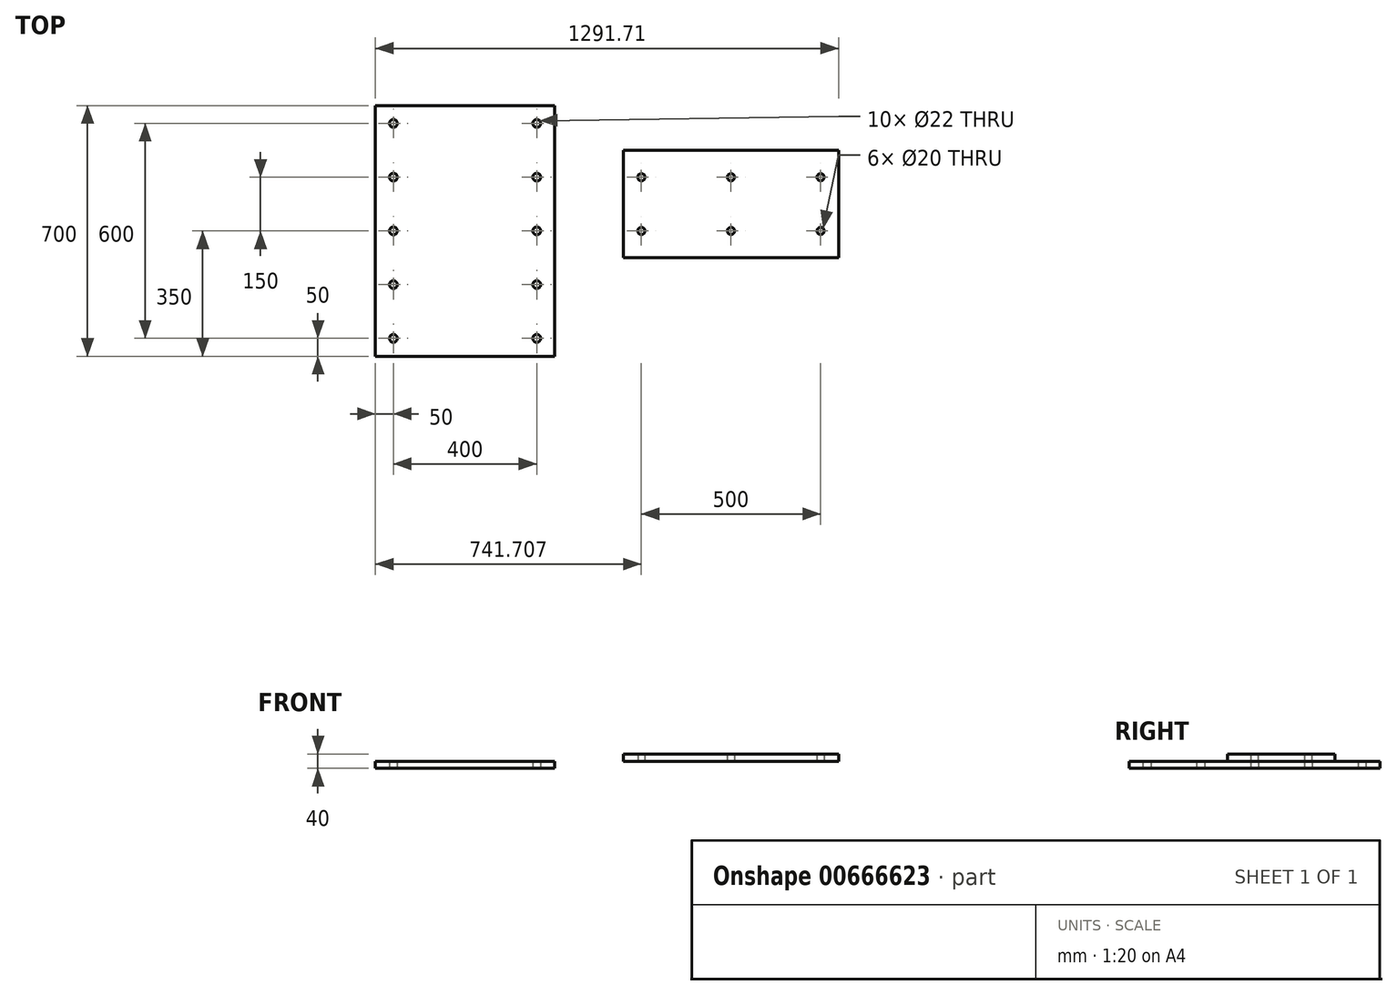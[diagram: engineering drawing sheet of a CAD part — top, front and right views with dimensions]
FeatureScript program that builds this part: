
annotation { "Feature Type Name" : "Feature", "Feature Type Description" : "" }
export const myFeature = defineFeature(function(context is Context, id is Id, definition is map)
    precondition{}
    {
        {
            var Q0;
            Q0=qCreatedBy(makeId("Top.planeOp"),FACE);
            var sketch = newSketch(context, id + "F0", { "sketchPlane" : qUnion([Q0])});
            skLineSegment(sketch, "E0.bottom", {"start": v(250, -350) * mm, "end": v(-250, -350) * mm});
            skLineSegment(sketch, "E0.top", {"start": v(250, 350) * mm, "end": v(-250, 350) * mm});
            skLineSegment(sketch, "E0.left", {"start": v(250, -350) * mm, "end": v(250, 350) * mm});
            skLineSegment(sketch, "E0.right", {"start": v(-250, -350) * mm, "end": v(-250, 350) * mm});
            skPoint(sketch, "E0.middle", {"position": v(0, 0) * mm});
            skSolve(sketch);
        }
        {
            var Q0;
            Q0=makeQuery(id+"F0.imprint","IMPRINT",FACE,{"disambiguationData":[TD([[makeQuery(id+"F0.imprint","IMPRINT",EDGE,{"derivedFrom":sQuery(id+"F0.wireOp",EDGE,"E0.bottom")}),-1.0]])]});
            var sketch = newSketch(context, id + "F1", { "sketchPlane" : qUnion([Q0])});
            skCircle(sketch, "E1", {"center": v(200, 300) * mm, "radius": 11 * mm});
            skCircle(sketch, "E2", {"center": v(200, 150) * mm, "radius": 11 * mm});
            skCircle(sketch, "E3", {"center": v(200, 0) * mm, "radius": 11 * mm});
            skCircle(sketch, "E4", {"center": v(200, -150) * mm, "radius": 11 * mm});
            skCircle(sketch, "E5", {"center": v(200, -300) * mm, "radius": 11 * mm});
            skCircle(sketch, "E6", {"center": v(-200, 300) * mm, "radius": 11 * mm});
            skCircle(sketch, "E7", {"center": v(-200, 150) * mm, "radius": 11 * mm});
            skCircle(sketch, "E8", {"center": v(-200, 0) * mm, "radius": 11 * mm});
            skCircle(sketch, "E9", {"center": v(-200, -150) * mm, "radius": 11 * mm});
            skCircle(sketch, "E10", {"center": v(-200, -300) * mm, "radius": 11 * mm});
            skSolve(sketch);
        }
        {
            var Q0;
            Q0=makeQuery(id+"F1.imprint","IMPRINT",FACE,{"disambiguationData":[TD([[makeQuery(id+"F1.imprint","IMPRINT",EDGE,{"derivedFrom":sQuery(id+"F1.wireOp",EDGE,"E1")}),-1.0]])]});
            extrude(context, id + "F2", {"entities" : qUnion([Q0]), "depth" : 20 * mm, "offsetDistance" : 25 * mm});
        }
        {
            var Q0;
            Q0=makeQuery(id+"F2.opExtrude","CAP_FACE",FACE,{"disambiguationData":[OSD([sQuery(id+"F0.wireOp",EDGE,"E0.bottom"),sQuery(id+"F0.wireOp",EDGE,"E0.top"),sQuery(id+"F0.wireOp",EDGE,"E0.left"),sQuery(id+"F0.wireOp",EDGE,"E0.right"),sQuery(id+"F1.wireOp",EDGE,"E1"),sQuery(id+"F1.wireOp",EDGE,"E2"),sQuery(id+"F1.wireOp",EDGE,"E3"),sQuery(id+"F1.wireOp",EDGE,"E4"),sQuery(id+"F1.wireOp",EDGE,"E5"),sQuery(id+"F1.wireOp",EDGE,"E6"),sQuery(id+"F1.wireOp",EDGE,"E7"),sQuery(id+"F1.wireOp",EDGE,"E8"),sQuery(id+"F1.wireOp",EDGE,"E9"),sQuery(id+"F1.wireOp",EDGE,"E10")])],"isStart":false});
            var sketch = newSketch(context, id + "F3", { "sketchPlane" : qUnion([Q0])});
            skLineSegment(sketch, "E11.bottom", {"start": v(441.7, 225) * mm, "end": v(1041.7, 225) * mm});
            skLineSegment(sketch, "E11.top", {"start": v(441.7, -75) * mm, "end": v(1041.7, -75) * mm});
            skLineSegment(sketch, "E11.left", {"start": v(441.7, 225) * mm, "end": v(441.7, -75) * mm});
            skLineSegment(sketch, "E11.right", {"start": v(1041.7, 225) * mm, "end": v(1041.7, -75) * mm});
            skCircle(sketch, "E12", {"center": v(991.7, 150) * mm, "radius": 10 * mm});
            skCircle(sketch, "E13", {"center": v(741.7, 150) * mm, "radius": 10 * mm});
            skCircle(sketch, "E14", {"center": v(491.7, 150) * mm, "radius": 10 * mm});
            skCircle(sketch, "E15", {"center": v(991.7, 0) * mm, "radius": 10 * mm});
            skCircle(sketch, "E16", {"center": v(741.7, 0) * mm, "radius": 10 * mm});
            skCircle(sketch, "E17", {"center": v(491.7, 0) * mm, "radius": 10 * mm});
            skSolve(sketch);
        }
        {
            var Q0;
            Q0=makeQuery(id+"F3.imprint","IMPRINT",FACE,{"disambiguationData":[TD([[makeQuery(id+"F3.imprint","IMPRINT",EDGE,{"derivedFrom":sQuery(id+"F3.wireOp",EDGE,"E11.bottom")}),-1.0]])]});
            extrude(context, id + "F4", {"entities" : qUnion([Q0]), "depth" : 20 * mm, "offsetDistance" : 25 * mm});
        }
    });
